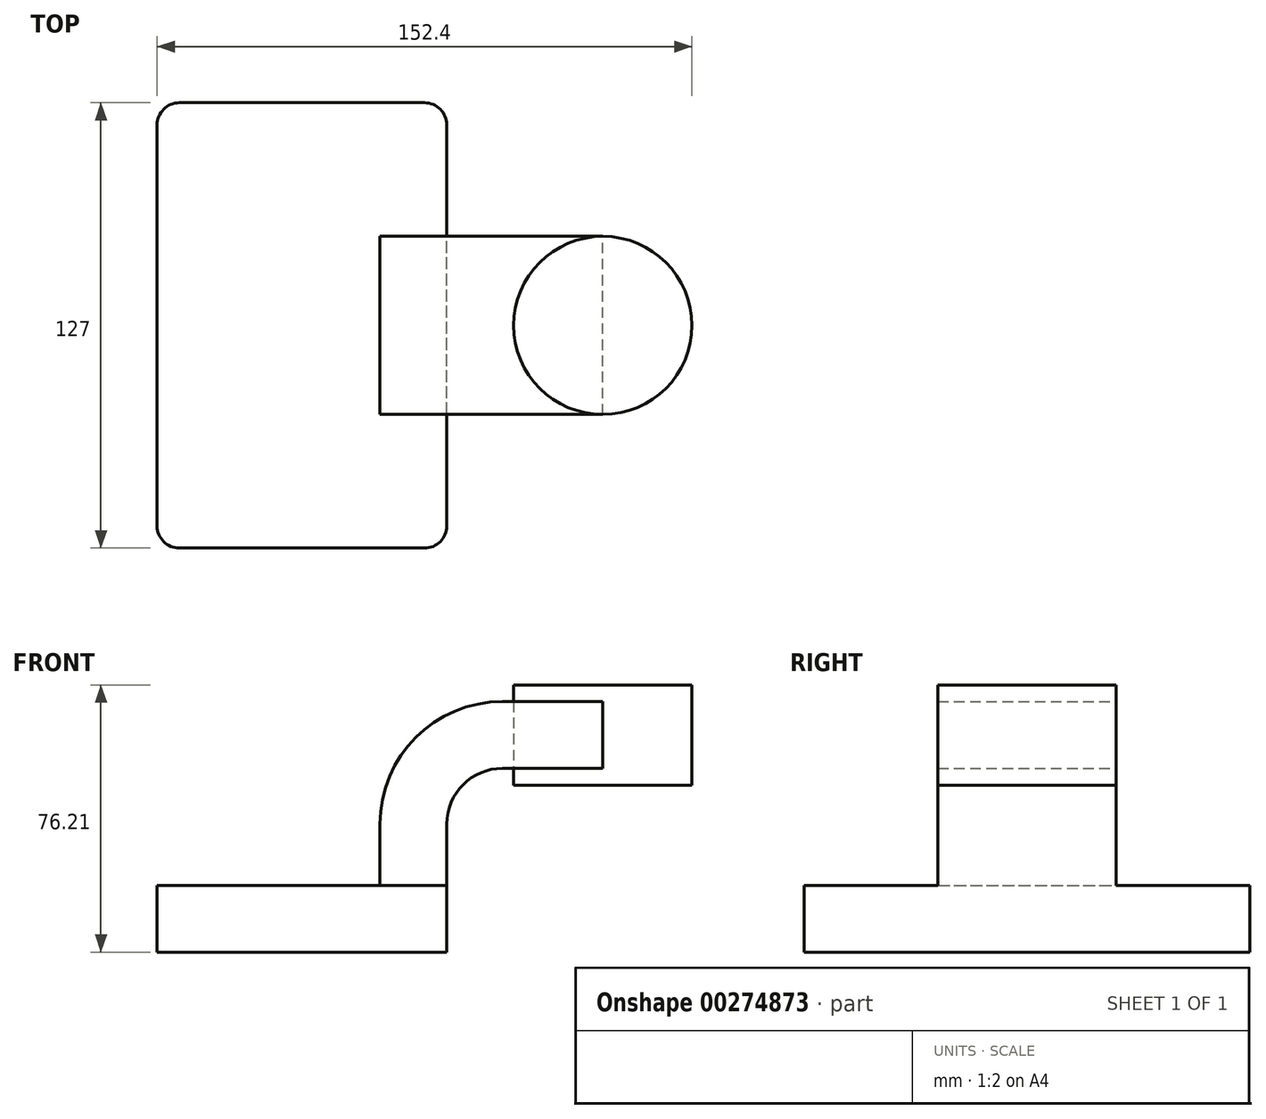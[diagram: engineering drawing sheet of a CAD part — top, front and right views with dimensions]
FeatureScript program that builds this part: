
annotation { "Feature Type Name" : "Feature", "Feature Type Description" : "" }
export const myFeature = defineFeature(function(context is Context, id is Id, definition is map)
    precondition{}
    {
        {
            var Q0;
            Q0=qCreatedBy(makeId("Front.planeOp"),FACE);
            var sketch = newSketch(context, id + "F0", { "sketchPlane" : qUnion([Q0])});
            skLineSegment(sketch, "E0.bottom", {"start": v(41.27, 9.53) * mm, "end": v(-41.28, 9.53) * mm});
            skLineSegment(sketch, "E0.top", {"start": v(41.28, -9.52) * mm, "end": v(-41.27, -9.52) * mm});
            skLineSegment(sketch, "E0.left", {"start": v(41.28, 9.53) * mm, "end": v(41.28, -9.52) * mm});
            skLineSegment(sketch, "E0.right", {"start": v(-41.28, 9.53) * mm, "end": v(-41.27, -9.52) * mm});
            skPoint(sketch, "E0.middle", {"position": v(0, 0) * mm});
            skLineSegment(sketch, "E1.bottom", {"start": v(111.13, 38.1) * mm, "end": v(60.33, 38.1) * mm});
            skLineSegment(sketch, "E1.top", {"start": v(111.13, 66.68) * mm, "end": v(60.33, 66.68) * mm});
            skLineSegment(sketch, "E1.left", {"start": v(111.13, 38.1) * mm, "end": v(111.13, 66.68) * mm});
            skLineSegment(sketch, "E1.right", {"start": v(60.33, 38.1) * mm, "end": v(60.33, 66.68) * mm});
            skPoint(sketch, "E1.middle", {"position": v(85.73, 52.39) * mm});
            skLineSegment(sketch, "E2", {"start": v(41.27, 9.53) * mm, "end": v(41.27, 27) * mm});
            skArc(sketch, "E3", {"start": v(41.27, 27) * mm, "mid": v(45.92, 38.23) * mm, "end": v(57.15, 42.88) * mm});
            skLineSegment(sketch, "E4", {"start": v(57.15, 42.88) * mm, "end": v(85.72, 42.88) * mm});
            skLineSegment(sketch, "E5.0", {"start": v(57.15, 61.93) * mm, "end": v(85.72, 61.93) * mm});
            skArc(sketch, "E5.1", {"start": v(22.23, 27) * mm, "mid": v(32.45, 51.7) * mm, "end": v(57.15, 61.93) * mm});
            skLineSegment(sketch, "E5.2", {"start": v(22.22, 9.53) * mm, "end": v(22.22, 27) * mm});
            skLineSegment(sketch, "E6", {"start": v(85.73, 38.1) * mm, "end": v(85.73, 66.68) * mm});
            skFitSpline(sketch, "E7", {"points": [v(60.33, 66.67) * mm, v(-41.28, 9.53) * mm], "startDerivative": vector(-110.16, -14.25) * mm, "endDerivative": vector(-81.96, -162.85) * mm});
            skSolve(sketch);
        }
        {
            var Q0;
            Q0=makeQuery(id+"F0.imprint","IMPRINT",FACE,{"disambiguationData":[TD([[makeQuery(id+"F0.imprint","IMPRINT",EDGE,{"derivedFrom":sQuery(id+"F0.wireOp",EDGE,"E0.top")}),-1.0]])]});
            extrude(context, id + "F1", {"entities" : qUnion([Q0]), "endBound" : BoundingType.SYMMETRIC, "depth" : 127 * mm});
        }
        {
            var Q0;
            {var subQ1=sQuery(id+"F0.wireOp",EDGE,"E2");Q0=makeQuery(id+"F0.imprint","IMPRINT",FACE,{"disambiguationData":[TD([[makeQuery(id+"F0.imprint","IMPRINT",EDGE,{"derivedFrom":subQ1}),1.0]])]});}
            var Q1;
            {var subQ0=sQuery(id+"F0.wireOp",EDGE,"E4");var subQ1=sQuery(id+"F0.wireOp",EDGE,"E1.right");var subQ2=makeQuery(id+"F0.imprint","INTERSECT",VERTEX,{"derivedFrom":[subQ1,subQ0]});Q1=makeQuery(id+"F0.imprint","IMPRINT",FACE,{"disambiguationData":[TD([[makeQuery(id+"F0.imprint","IMPRINT",EDGE,{"disambiguationData":[TD([[subQ2,-1.0]])],"derivedFrom":subQ1}),-1.0]])]});}
            var Q2;
            Q2=sQuery(id+"F0.wireOp",EDGE,"E7");
            var Q3;
            Q3=sQuery(id+"F0.wireOp",EDGE,"E5.1");
            extrude(context, id + "F2", {"entities" : qUnion([Q0, Q1]), "operationType" : NewBodyOperationType.ADD, "surfaceEntities" : qUnion([Q2, Q3]), "endBound" : BoundingType.SYMMETRIC, "depth" : 50.8 * mm});
        }
        {
            var Q0;
            {var subQ0=sQuery(id+"F0.wireOp",EDGE,"E5.1");Q0=makeQuery(id+"F0.imprint","IMPRINT",FACE,{"disambiguationData":[TD([[makeQuery(id+"F0.imprint","IMPRINT",EDGE,{"derivedFrom":subQ0}),1.0]])]});}
            extrude(context, id + "F3", {"entities" : qUnion([Q0]), "operationType" : NewBodyOperationType.ADD, "endBound" : BoundingType.SYMMETRIC, "depth" : 15.88 * mm});
        }
        {
            var Q0;
            {var subQ0=sQuery(id+"F0.wireOp",EDGE,"E1.left");Q0=makeQuery(id+"F0.imprint","IMPRINT",FACE,{"disambiguationData":[TD([[makeQuery(id+"F0.imprint","IMPRINT",EDGE,{"derivedFrom":subQ0}),1.0]])]});}
            var Q1;
            Q1=sQuery(id+"F0.wireOp",EDGE,"E6");
            revolve(context, id + "F4", {"entities" : qUnion([Q0]), "axis" : qUnion([Q1]), "revolveType" : RevolveType.FULL});
        }
        {
            var Q0;
            Q0=makeQuery(id+"F1.opExtrude","CAP_EDGE",EDGE,{"disambiguationData":[OSD([sQuery(id+"F0.wireOp",EDGE,"E0.left")])],"isStart":false});
            var Q1;
            Q1=makeQuery(id+"F1.opExtrude","CAP_EDGE",EDGE,{"disambiguationData":[OSD([sQuery(id+"F0.wireOp",EDGE,"E0.right")])],"isStart":false});
            var Q2;
            Q2=makeQuery(id+"F1.opExtrude","CAP_EDGE",EDGE,{"disambiguationData":[OSD([sQuery(id+"F0.wireOp",EDGE,"E0.right")])],"isStart":true});
            var Q3;
            Q3=makeQuery(id+"F1.opExtrude","CAP_EDGE",EDGE,{"disambiguationData":[OSD([sQuery(id+"F0.wireOp",EDGE,"E0.left")])],"isStart":true});
            fillet(context, id + "F5", {"entities" : qUnion([Q0, Q1, Q2, Q3]), "radius" : 6.35 * mm, "tangentPropagation" : true, "allowEdgeOverflow" : false});
        }
    });
